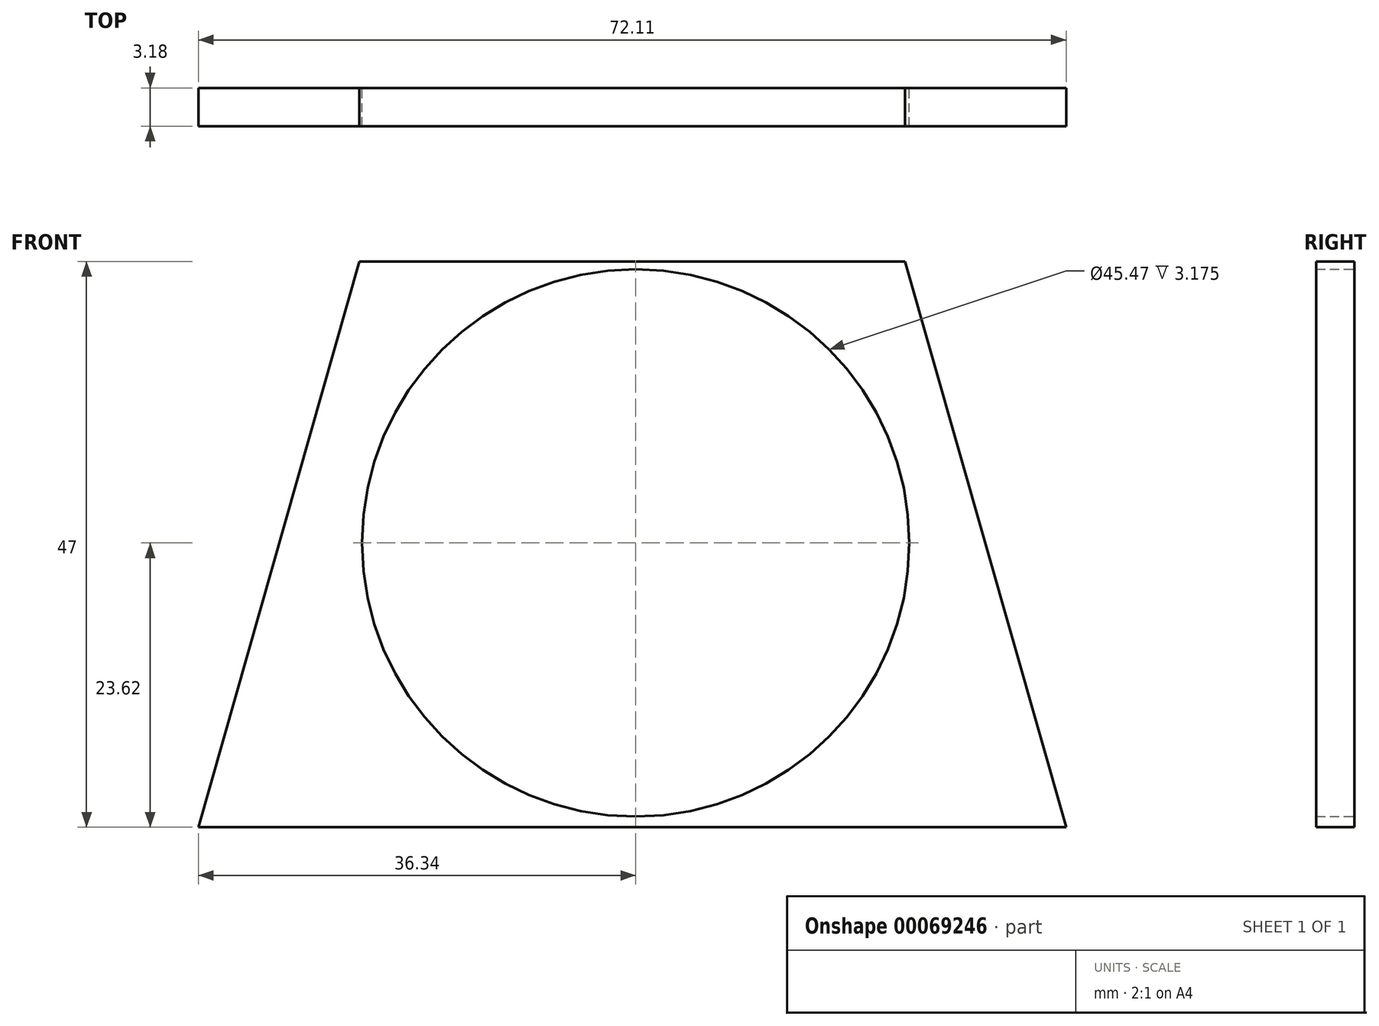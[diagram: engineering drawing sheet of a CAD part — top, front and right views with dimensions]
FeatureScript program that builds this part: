
annotation { "Feature Type Name" : "Feature", "Feature Type Description" : "" }
export const myFeature = defineFeature(function(context is Context, id is Id, definition is map)
    precondition{}
    {
        {
            var Q0;
            Q0=qCreatedBy(makeId("Front.planeOp"),FACE);
            var sketch = newSketch(context, id + "F0", { "sketchPlane" : qUnion([Q0])});
            skLineSegment(sketch, "E0", {"start": v(-22.95, 23.38) * mm, "end": v(22.38, 23.38) * mm});
            skLineSegment(sketch, "E1", {"start": v(-36.34, -23.62) * mm, "end": v(35.77, -23.62) * mm});
            skLineSegment(sketch, "E2", {"start": v(22.38, 23.38) * mm, "end": v(35.77, -23.62) * mm});
            skLineSegment(sketch, "E3", {"start": v(-22.95, 23.38) * mm, "end": v(-36.34, -23.62) * mm});
            skCircle(sketch, "E4", {"center": v(0, 0) * mm, "radius": 22.73 * mm});
            skSolve(sketch);
        }
        {
            var Q0;
            Q0=makeQuery(id+"F0.imprint","IMPRINT",FACE,{"disambiguationData":[TD([[makeQuery(id+"F0.imprint","IMPRINT",EDGE,{"derivedFrom":sQuery(id+"F0.wireOp",EDGE,"wso3QenZ-duVl-f2pc-Tnpq-ScvSmjJ3Tjyx")}),-1.0]])]});
            var Q1;
            Q1=makeQuery(id+"F0.imprint","IMPRINT",FACE,{"disambiguationData":[TD([[makeQuery(id+"F0.imprint","IMPRINT",EDGE,{"derivedFrom":sQuery(id+"F0.wireOp",EDGE,"E0")}),-1.0]])]});
            extrude(context, id + "F1", {"entities" : qUnion([Q0, Q1]), "endBound" : BoundingType.SYMMETRIC, "depth" : 3.17 * mm});
        }
    });
